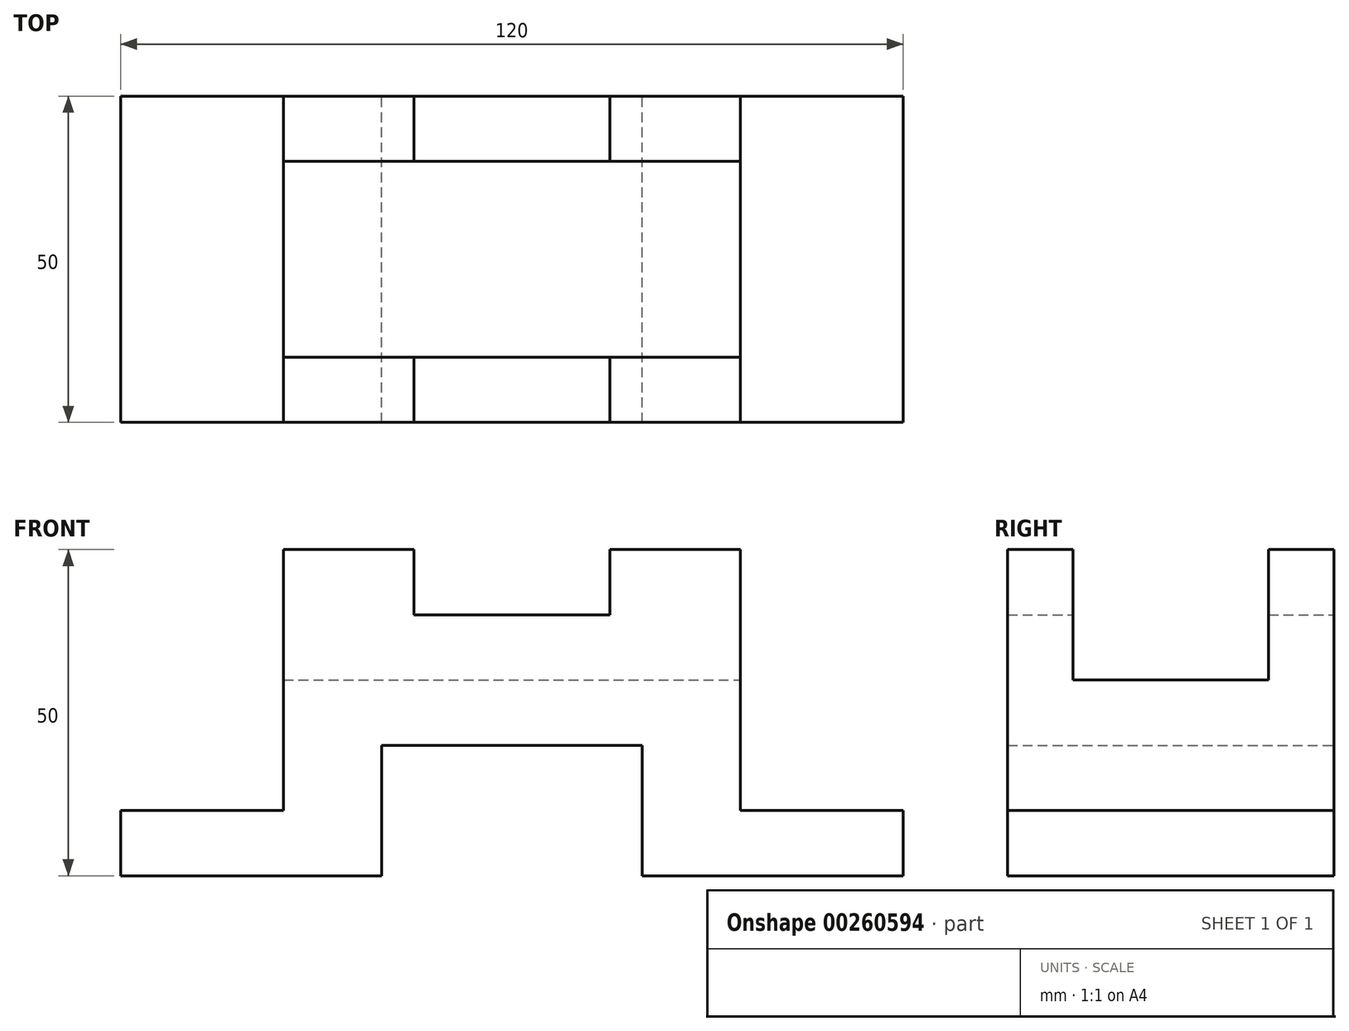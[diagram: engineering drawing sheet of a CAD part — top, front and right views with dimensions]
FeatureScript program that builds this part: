
annotation { "Feature Type Name" : "Feature", "Feature Type Description" : "" }
export const myFeature = defineFeature(function(context is Context, id is Id, definition is map)
    precondition{}
    {
        {
            assignVariable(context, id + "F0", {"name" : "A", "anyValue" : 50});
        }
        {
            var Q0;
            Q0=qCreatedBy(makeId("Front.planeOp"),FACE);
            var sketch = newSketch(context, id + "F1", { "sketchPlane" : qUnion([Q0])});
            skLineSegment(sketch, "E0", {"start": v(-40, 20) * mm, "end": v(-40, 0) * mm});
            skLineSegment(sketch, "E1", {"start": v(-40, 0) * mm, "end": v(-80, 0) * mm});
            skLineSegment(sketch, "E2", {"start": v(-80, 0) * mm, "end": v(-80, 10) * mm});
            skLineSegment(sketch, "E3", {"start": v(-80, 10) * mm, "end": v(-55, 10) * mm});
            skLineSegment(sketch, "E4", {"start": v(-55, 10) * mm, "end": v(-55, 50) * mm});
            skLineSegment(sketch, "E5", {"start": v(-55, 50) * mm, "end": v(-35, 50) * mm});
            skLineSegment(sketch, "E6", {"start": v(-35, 50) * mm, "end": v(-35, 40) * mm});
            skLineSegment(sketch, "E7", {"start": v(15, 50) * mm, "end": v(15, 10) * mm});
            skLineSegment(sketch, "E8", {"start": v(15, 10) * mm, "end": v(40, 10) * mm});
            skLineSegment(sketch, "E9", {"start": v(40, 10) * mm, "end": v(40, 0) * mm});
            skLineSegment(sketch, "E10", {"start": v(40, 0) * mm, "end": v(0, 0) * mm});
            skLineSegment(sketch, "E11", {"start": v(-40, 20) * mm, "end": v(0, 20) * mm});
            skLineSegment(sketch, "E12", {"start": v(0, 20) * mm, "end": v(0, 0) * mm});
            skLineSegment(sketch, "E13", {"start": v(-35, 40) * mm, "end": v(-5, 40) * mm});
            skLineSegment(sketch, "E14", {"start": v(-5, 40) * mm, "end": v(-5, 49.98) * mm});
            skLineSegment(sketch, "E15", {"start": v(-5, 49.98) * mm, "end": v(15, 50) * mm});
            skSolve(sketch);
        }
        {
            var Q0;
            Q0=makeQuery(id+"F1.imprint","IMPRINT",FACE,{"disambiguationData":[TD([[makeQuery(id+"F1.imprint","IMPRINT",EDGE,{"derivedFrom":sQuery(id+"F1.wireOp",EDGE,"E0")}),-1.0]])]});
            extrude(context, id + "F2", {"entities" : qUnion([Q0]), "depth" : getVariable(context, 'A') * mm});
        }
        {
            var Q0;
            Q0=makeQuery(id+"F2.opExtrude","SWEPT_FACE",FACE,{"disambiguationData":[OSD([sQuery(id+"F1.wireOp",EDGE,"E5")])]});
            var sketch = newSketch(context, id + "F3", { "sketchPlane" : qUnion([Q0])});
            skLineSegment(sketch, "E16.top", {"start": v(-55, -10) * mm, "end": v(15, -10) * mm});
            skLineSegment(sketch, "E17.top", {"start": v(-55, -40) * mm, "end": v(15, -40) * mm});
            skLineSegment(sketch, "E17.left", {"start": v(-55, -10) * mm, "end": v(-55, -40) * mm});
            skLineSegment(sketch, "E17.right", {"start": v(15, -10) * mm, "end": v(15, -40) * mm});
            skSolve(sketch);
        }
        {
            var Q0;
            {var subQ0=sQuery(id+"F3.wireOp",EDGE,"E17.left");Q0=makeQuery(id+"F3.imprint","IMPRINT",FACE,{"disambiguationData":[TD([[makeQuery(id+"F3.imprint","IMPRINT",EDGE,{"derivedFrom":subQ0}),-1.0]])]});}
            var Q1;
            {var subQ0=sQuery(id+"F3.wireOp",EDGE,"E17.right");Q1=makeQuery(id+"F3.imprint","IMPRINT",FACE,{"disambiguationData":[TD([[makeQuery(id+"F3.imprint","IMPRINT",EDGE,{"derivedFrom":subQ0}),-1.0]])]});}
            extrude(context, id + "F4", {"entities" : qUnion([Q0, Q1]), "operationType" : NewBodyOperationType.REMOVE, "oppositeDirection" : true, "depth" : 20 * mm});
        }
    });
